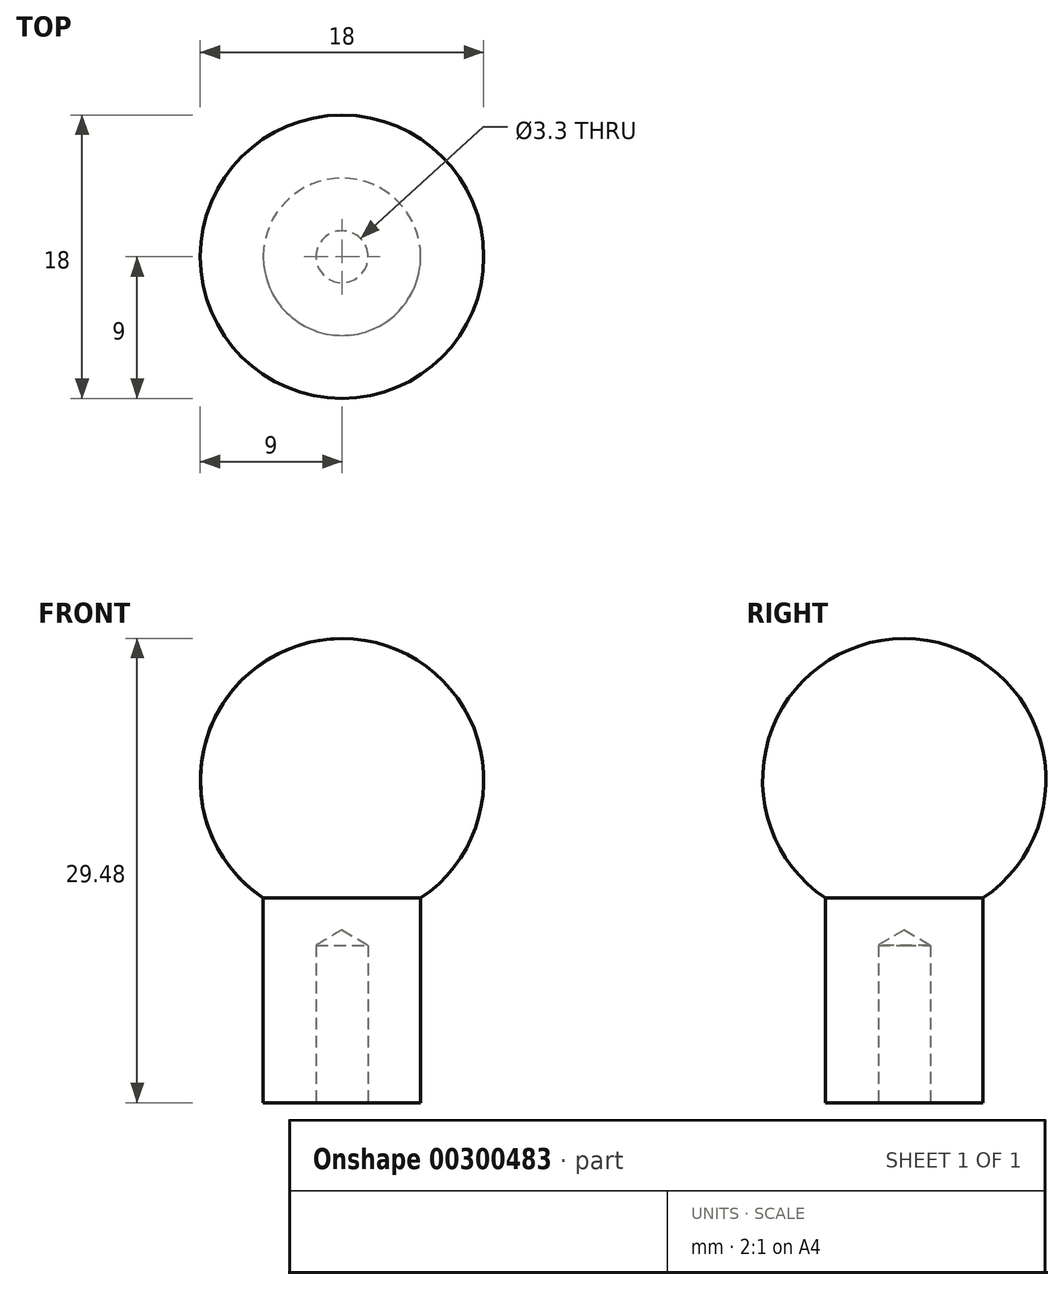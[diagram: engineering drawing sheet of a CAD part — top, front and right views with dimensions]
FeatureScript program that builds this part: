
annotation { "Feature Type Name" : "Feature", "Feature Type Description" : "" }
export const myFeature = defineFeature(function(context is Context, id is Id, definition is map)
    precondition{}
    {
        {
            var Q0;
            Q0=qCreatedBy(makeId("Front.planeOp"),FACE);
            var sketch = newSketch(context, id + "F0", { "sketchPlane" : qUnion([Q0])});
            skArc(sketch, "E0", {"start": v(0, 9) * mm, "mid": v(-9, 0) * mm, "end": v(0, -9) * mm});
            skLineSegment(sketch, "E1", {"start": v(0, 0) * mm, "end": v(0, -20.48) * mm});
            skLineSegment(sketch, "E2", {"start": v(0, -20.48) * mm, "end": v(-5, -20.48) * mm});
            skLineSegment(sketch, "E3", {"start": v(-5, -20.48) * mm, "end": v(-5, -7.48) * mm});
            skLineSegment(sketch, "E4", {"start": v(0, 0) * mm, "end": v(0, 9) * mm});
            skSolve(sketch);
        }
        {
            var Q0;
            {var subQ0=sQuery(id+"F0.wireOp",EDGE,"E4");Q0=makeQuery(id+"F0.imprint","IMPRINT",FACE,{"disambiguationData":[TD([[makeQuery(id+"F0.imprint","IMPRINT",EDGE,{"derivedFrom":subQ0}),1.0]])]});}
            var Q1;
            {var subQ4=sQuery(id+"F0.wireOp",EDGE,"E2");Q1=makeQuery(id+"F0.imprint","IMPRINT",FACE,{"disambiguationData":[TD([[makeQuery(id+"F0.imprint","IMPRINT",EDGE,{"derivedFrom":subQ4}),-1.0]])]});}
            var Q2;
            Q2=sQuery(id+"F0.wireOp",EDGE,"E1");
            revolve(context, id + "F1", {"entities" : qUnion([Q0, Q1]), "axis" : qUnion([Q2]), "revolveType" : RevolveType.FULL});
        }
        {
            var Q0;
            Q0=makeQuery(id+"F1.opRevolve","SWEPT_FACE",FACE,{"disambiguationData":[OSD([sQuery(id+"F0.wireOp",EDGE,"E2")])]});
            var sketch = newSketch(context, id + "F2", { "sketchPlane" : qUnion([Q0])});
            skLineSegment(sketch, "E5", {"start": v(0, 0) * mm, "end": v(5, 0) * mm});
            skSolve(sketch);
        }
        {
            var Q0;
            Q0=sQuery(id+"F2.wireOp",VERTEX,"E5.start");
            var Q1;
            Q1=makeQuery(id+"F1.opRevolve","SWEPT_BODY",BODY,{"disambiguationData":[OSD([sQuery(id+"F0.wireOp",EDGE,"E0"),sQuery(id+"F0.wireOp",EDGE,"E1"),sQuery(id+"F0.wireOp",EDGE,"E2"),sQuery(id+"F0.wireOp",EDGE,"E3"),sQuery(id+"F0.wireOp",EDGE,"E4")])]});
            hole(context, id + "F3", {"style" : HoleStyle.SIMPLE, "endStyle" : HoleEndStyle.BLIND, "holeDiameter" : 3.3 * mm, "holeDepth" : 10 * mm, "tappedDepth" : 12 * mm, "tapClearance" : 3, "locations" : qUnion([Q0]), "scope" : qUnion([Q1])});
        }
    });
